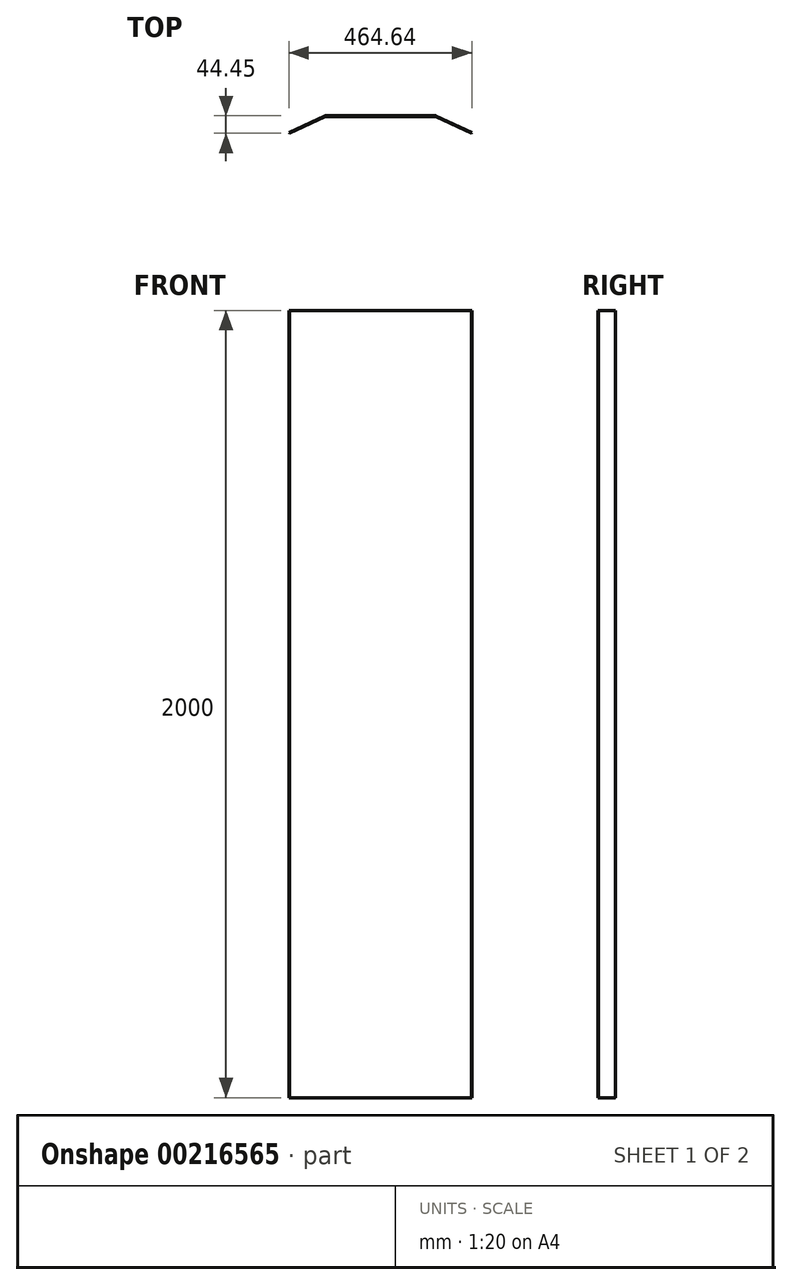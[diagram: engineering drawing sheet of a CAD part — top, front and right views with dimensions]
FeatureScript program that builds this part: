
annotation { "Feature Type Name" : "Feature", "Feature Type Description" : "" }
export const myFeature = defineFeature(function(context is Context, id is Id, definition is map)
    precondition{}
    {
        {
            var Q0;
            Q0=qCreatedBy(makeId("Top.planeOp"),FACE);
            var sketch = newSketch(context, id + "F0", { "sketchPlane" : qUnion([Q0])});
            skLineSegment(sketch, "E0", {"start": v(0, 1) * mm, "end": v(-140, 1) * mm});
            skCircle(sketch, "E1", {"center": v(0, 0) * mm, "radius": 1 * mm, "construction": true});
            skLineSegment(sketch, "E2", {"start": v(0, -1) * mm, "end": v(-140, -1) * mm});
            skLineSegment(sketch, "E3", {"start": v(-140, 8.85) * mm, "end": v(-140, -25.3) * mm, "construction": true});
            skLineSegment(sketch, "E4", {"start": v(-131.61, -3) * mm, "end": v(-149.4, -3) * mm, "construction": true});
            skLineSegment(sketch, "E5", {"start": v(-140.85, -1.19) * mm, "end": v(-231.48, -43.45) * mm});
            skLineSegment(sketch, "E6", {"start": v(-232.32, -41.64) * mm, "end": v(-231.48, -43.45) * mm});
            skLineSegment(sketch, "E7", {"start": v(-232.32, -41.64) * mm, "end": v(-141.7, 0.63) * mm});
            skArc(sketch, "E8.trimOffspring", {"start": v(-140, 1) * mm, "mid": v(-140.87, 0.9) * mm, "end": v(-141.7, 0.63) * mm});
            skArc(sketch, "E9.trimOffspring", {"start": v(-140, -1) * mm, "mid": v(-140.43, -1.05) * mm, "end": v(-140.85, -1.19) * mm});
            skArc(sketch, "E10.MirrorCS", {"start": v(140, 1) * mm, "mid": v(140.87, 0.9) * mm, "end": v(141.7, 0.63) * mm});
            skArc(sketch, "E11.MirrorCS", {"start": v(140, -1) * mm, "mid": v(140.43, -1.05) * mm, "end": v(140.85, -1.19) * mm});
            skLineSegment(sketch, "E12.MirrorCS", {"start": v(232.32, -41.64) * mm, "end": v(231.48, -43.45) * mm});
            skLineSegment(sketch, "E13.MirrorCS", {"start": v(140.85, -1.19) * mm, "end": v(231.48, -43.45) * mm});
            skLineSegment(sketch, "E14.MirrorCS", {"start": v(131.61, -3) * mm, "end": v(149.4, -3) * mm, "construction": true});
            skLineSegment(sketch, "E15.MirrorCS", {"start": v(232.32, -41.64) * mm, "end": v(141.7, 0.63) * mm});
            skLineSegment(sketch, "E16.MirrorCS", {"start": v(140, 8.85) * mm, "end": v(140, -25.3) * mm, "construction": true});
            skLineSegment(sketch, "E17.MirrorCS", {"start": v(0, 1) * mm, "end": v(140, 1) * mm});
            skLineSegment(sketch, "E18.MirrorCS", {"start": v(0, -1) * mm, "end": v(140, -1) * mm});
            skSolve(sketch);
        }
        {
            var Q0;
            Q0 = qSketchRegion(id + "F0", true);
            extrude(context, id + "F1", {"entities" : qUnion([Q0]), "depth" : 2000 * mm});
        }
    });
